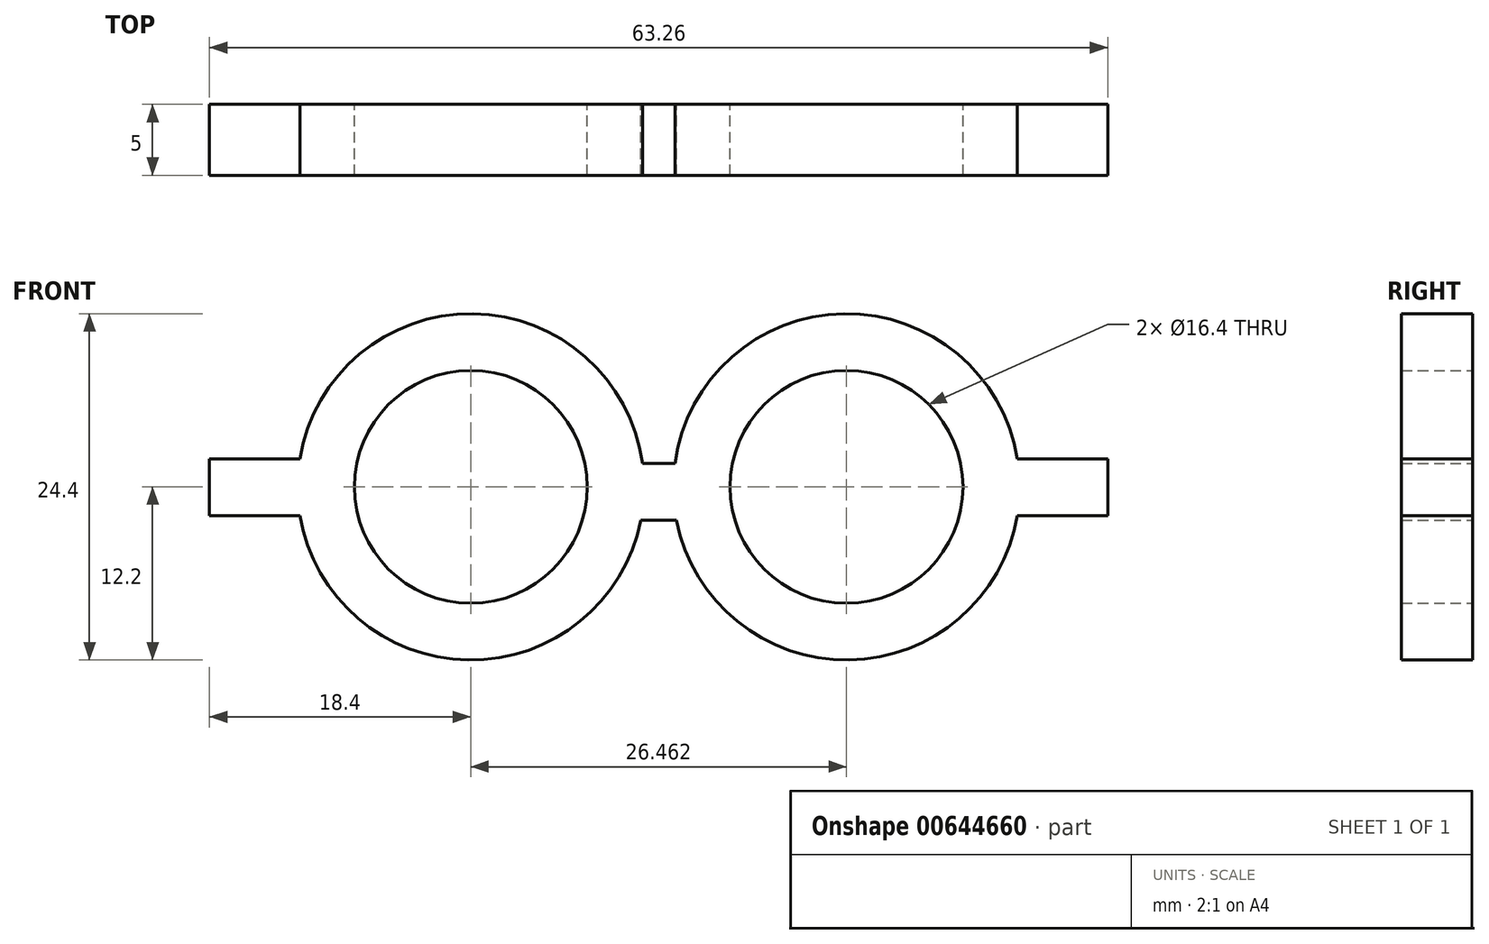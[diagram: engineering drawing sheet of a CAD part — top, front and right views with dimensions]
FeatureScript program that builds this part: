
annotation { "Feature Type Name" : "Feature", "Feature Type Description" : "" }
export const myFeature = defineFeature(function(context is Context, id is Id, definition is map)
    precondition{}
    {
        {
            var Q0;
            Q0=qCreatedBy(makeId("Front.planeOp"),FACE);
            var sketch = newSketch(context, id + "F0", { "sketchPlane" : qUnion([Q0])});
            skCircle(sketch, "E0", {"center": v(0, 0) * mm, "radius": 8.2 * mm});
            skArc(sketch, "E1", {"start": v(-12.03, -2.02) * mm, "mid": v(-0.17, -12.2) * mm, "end": v(11.97, -2.35) * mm});
            skCircle(sketch, "E2.1.0.0", {"center": v(26.46, 0) * mm, "radius": 8.2 * mm});
            skArc(sketch, "E2.1.0.1", {"start": v(38.5, 1.98) * mm, "mid": v(26.3, 12.2) * mm, "end": v(14.37, 1.65) * mm});
            skLineSegment(sketch, "E2.direction1", {"start": v(0, 0) * mm, "end": v(8.2, 0) * mm, "construction": true});
            skLineSegment(sketch, "E3.bottom", {"start": v(38.5, 1.98) * mm, "end": v(44.86, 1.98) * mm});
            skLineSegment(sketch, "E3.left", {"start": v(26.46, 0) * mm, "end": v(26.46, -2.02) * mm});
            skLineSegment(sketch, "E3.right", {"start": v(44.86, 1.98) * mm, "end": v(44.86, -2.02) * mm});
            skPoint(sketch, "E4.oppositeSnap0", {"position": v(35.66, -2.02) * mm});
            skLineSegment(sketch, "E4.right", {"start": v(-18.4, 1.98) * mm, "end": v(-18.4, -2.02) * mm});
            skLineSegment(sketch, "E5.bottom", {"start": v(12.09, 1.65) * mm, "end": v(14.37, 1.65) * mm});
            skLineSegment(sketch, "E5.top", {"start": v(11.97, -2.35) * mm, "end": v(14.5, -2.35) * mm});
            skPoint(sketch, "E6.orphan", {"position": v(26.46, 1.98) * mm});
            skLineSegment(sketch, "E7.trimOffspring", {"start": v(-12.04, 1.98) * mm, "end": v(-18.4, 1.98) * mm});
            skLineSegment(sketch, "E8.trimOffspring", {"start": v(-12.03, -2.02) * mm, "end": v(-18.4, -2.02) * mm});
            skPoint(sketch, "E4.bottom.start.orphan", {"position": v(0, 1.98) * mm});
            skArc(sketch, "E9.trimOffspring", {"start": v(12.09, 1.65) * mm, "mid": v(0.17, 12.2) * mm, "end": v(-12.04, 1.98) * mm});
            skArc(sketch, "E10.trimOffspring", {"start": v(14.5, -2.35) * mm, "mid": v(26.63, -12.2) * mm, "end": v(38.5, -2.02) * mm});
            skLineSegment(sketch, "E11.trimOffspring", {"start": v(9.8, 0) * mm, "end": v(26.46, 0) * mm, "construction": true});
            skLineSegment(sketch, "E12.trimOffspring", {"start": v(38.5, -2.02) * mm, "end": v(44.86, -2.02) * mm});
            skSolve(sketch);
        }
        {
            var Q0;
            Q0=makeQuery(id+"F0.imprint","IMPRINT",FACE,{"disambiguationData":[TD([[makeQuery(id+"F0.imprint","IMPRINT",EDGE,{"derivedFrom":sQuery(id+"F0.wireOp",EDGE,"E0")}),-1.0]])]});
            extrude(context, id + "F1", {"entities" : qUnion([Q0]), "depth" : 5 * mm, "offsetDistance" : 25 * mm});
        }
    });
